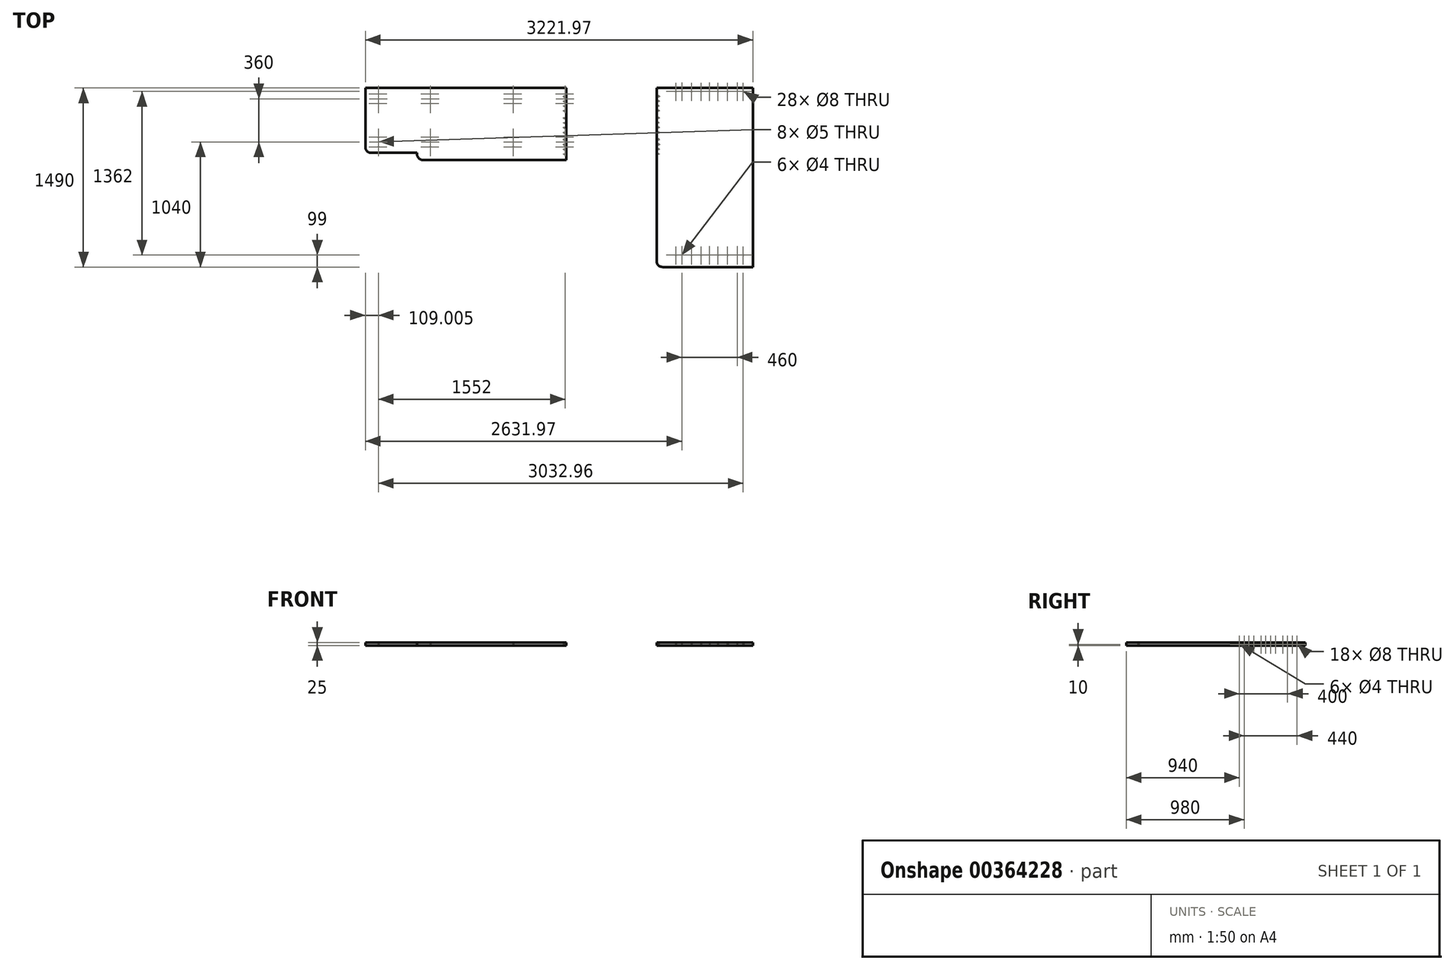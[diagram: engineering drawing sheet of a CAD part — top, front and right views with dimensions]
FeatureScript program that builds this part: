
annotation { "Feature Type Name" : "Feature", "Feature Type Description" : "" }
export const myFeature = defineFeature(function(context is Context, id is Id, definition is map)
    precondition{}
    {
        {
            var Q0;
            Q0=qCreatedBy(makeId("Top.planeOp"),FACE);
            var sketch = newSketch(context, id + "F0", { "sketchPlane" : qUnion([Q0])});
            skLineSegment(sketch, "E0.bottom", {"start": v(-2341.59, 0) * mm, "end": v(-671.59, 0) * mm});
            skLineSegment(sketch, "E0.left", {"start": v(-2341.59, 0) * mm, "end": v(-2341.59, -490) * mm});
            skLineSegment(sketch, "E0.right", {"start": v(-671.59, 0) * mm, "end": v(-671.59, -600) * mm});
            skLineSegment(sketch, "E1", {"start": v(-671.59, -600) * mm, "end": v(-1861.59, -600) * mm});
            skLineSegment(sketch, "E2", {"start": v(-2291.59, -540) * mm, "end": v(-1911.59, -540) * mm});
            skLineSegment(sketch, "E3", {"start": v(-1911.59, -540) * mm, "end": v(-1911.59, -550) * mm});
            skPoint(sketch, "E4.visualSharp", {"position": v(-2341.59, -540) * mm});
            skArc(sketch, "E4.filletArc", {"start": v(-2341.59, -490) * mm, "mid": v(-2326.94, -525.36) * mm, "end": v(-2291.59, -540) * mm});
            skPoint(sketch, "E5.visualSharp", {"position": v(-1911.59, -600) * mm});
            skArc(sketch, "E5.filletArc", {"start": v(-1911.59, -550) * mm, "mid": v(-1896.94, -585.36) * mm, "end": v(-1861.59, -600) * mm});
            skLineSegment(sketch, "E6", {"start": v(0, 0) * mm, "end": v(-671.59, 0) * mm, "construction": true});
            skSolve(sketch);
        }
        {
            var Q0;
            Q0=qCreatedBy(makeId("Top.planeOp"),FACE);
            var sketch = newSketch(context, id + "F1", { "sketchPlane" : qUnion([Q0])});
            skLineSegment(sketch, "E7.bottom", {"start": v(80.38, 0) * mm, "end": v(880.38, 0) * mm});
            skLineSegment(sketch, "E7.top", {"start": v(130.38, -1490) * mm, "end": v(880.38, -1490) * mm});
            skLineSegment(sketch, "E7.left", {"start": v(80.38, 0) * mm, "end": v(80.38, -1440) * mm});
            skLineSegment(sketch, "E7.right", {"start": v(880.38, 0) * mm, "end": v(880.38, -1490) * mm});
            skPoint(sketch, "E8.visualSharp", {"position": v(80.38, -1490) * mm});
            skArc(sketch, "E8.filletArc", {"start": v(80.38, -1440) * mm, "mid": v(95.02, -1475.36) * mm, "end": v(130.38, -1490) * mm});
            skLineSegment(sketch, "E9", {"start": v(0, 0) * mm, "end": v(80.38, 0) * mm, "construction": true});
            skSolve(sketch);
        }
        {
            var Q0;
            Q0=makeQuery(id+"F0.imprint","IMPRINT",FACE,{"disambiguationData":[TD([[makeQuery(id+"F0.imprint","IMPRINT",EDGE,{"derivedFrom":sQuery(id+"F0.wireOp",EDGE,"E0.bottom")}),-1.0]])]});
            extrude(context, id + "F2", {"entities" : qUnion([Q0]), "depth" : 25 * mm});
        }
        {
            var Q0;
            Q0 = qSketchRegion(id + "F1", true);
            extrude(context, id + "F3", {"entities" : qUnion([Q0]), "depth" : 25 * mm});
        }
        {
            var Q0;
            Q0=makeQuery(id+"F2.opExtrude","CAP_FACE",FACE,{"disambiguationData":[OSD([sQuery(id+"F0.wireOp",EDGE,"E0.bottom"),sQuery(id+"F0.wireOp",EDGE,"E0.left"),sQuery(id+"F0.wireOp",EDGE,"E0.right"),sQuery(id+"F0.wireOp",EDGE,"E1"),sQuery(id+"F0.wireOp",EDGE,"E2"),sQuery(id+"F0.wireOp",EDGE,"E3"),sQuery(id+"F0.wireOp",EDGE,"E4.filletArc"),sQuery(id+"F0.wireOp",EDGE,"E5.filletArc")])],"isStart":true});
            var sketch = newSketch(context, id + "F4", { "sketchPlane" : qUnion([Q0])});
            skLineSegment(sketch, "E10", {"start": v(-680.59, 600) * mm, "end": v(-680.59, 0) * mm, "construction": true});
            skPoint(sketch, "E11", {"position": v(-680.59, 50) * mm});
            skPoint(sketch, "E12.0.1.0", {"position": v(-680.59, 90) * mm});
            skPoint(sketch, "E12.0.2.0", {"position": v(-680.59, 130) * mm});
            skPoint(sketch, "E12.1.0.0", {"position": v(-1112.59, 50) * mm});
            skPoint(sketch, "E12.1.1.0", {"position": v(-1112.59, 90) * mm});
            skPoint(sketch, "E12.1.2.0", {"position": v(-1112.59, 130) * mm});
            skLineSegment(sketch, "E12.direction1", {"start": v(-680.59, 50) * mm, "end": v(-1112.59, 50) * mm, "construction": true});
            skLineSegment(sketch, "E12.direction2", {"start": v(-680.59, 50) * mm, "end": v(-680.59, 90) * mm, "construction": true});
            skLineSegment(sketch, "E13.0.1.0", {"start": v(-680.59, 410) * mm, "end": v(-1112.59, 410) * mm, "construction": true});
            skLineSegment(sketch, "E13.0.1.1", {"start": v(-680.59, 410) * mm, "end": v(-680.59, 450) * mm, "construction": true});
            skPoint(sketch, "E13.0.1.2", {"position": v(-680.59, 410) * mm});
            skPoint(sketch, "E13.0.1.3", {"position": v(-680.59, 450) * mm});
            skPoint(sketch, "E13.0.1.4", {"position": v(-680.59, 490) * mm});
            skPoint(sketch, "E13.0.1.5", {"position": v(-1112.59, 410) * mm});
            skPoint(sketch, "E13.0.1.6", {"position": v(-1112.59, 450) * mm});
            skPoint(sketch, "E13.0.1.7", {"position": v(-1112.59, 490) * mm});
            skLineSegment(sketch, "E13.1.0.0", {"start": v(-1800.59, 50) * mm, "end": v(-2232.59, 50) * mm, "construction": true});
            skLineSegment(sketch, "E13.1.0.1", {"start": v(-1800.59, 50) * mm, "end": v(-1800.59, 90) * mm, "construction": true});
            skPoint(sketch, "E13.1.0.2", {"position": v(-1800.59, 50) * mm});
            skPoint(sketch, "E13.1.0.3", {"position": v(-1800.59, 90) * mm});
            skPoint(sketch, "E13.1.0.4", {"position": v(-1800.59, 130) * mm});
            skPoint(sketch, "E13.1.0.5", {"position": v(-2232.59, 50) * mm});
            skPoint(sketch, "E13.1.0.6", {"position": v(-2232.59, 90) * mm});
            skPoint(sketch, "E13.1.0.7", {"position": v(-2232.59, 130) * mm});
            skLineSegment(sketch, "E13.1.1.0", {"start": v(-1800.59, 410) * mm, "end": v(-2232.59, 410) * mm, "construction": true});
            skLineSegment(sketch, "E13.1.1.1", {"start": v(-1800.59, 410) * mm, "end": v(-1800.59, 450) * mm, "construction": true});
            skPoint(sketch, "E13.1.1.2", {"position": v(-1800.59, 410) * mm});
            skPoint(sketch, "E13.1.1.3", {"position": v(-1800.59, 450) * mm});
            skPoint(sketch, "E13.1.1.4", {"position": v(-1800.59, 490) * mm});
            skPoint(sketch, "E13.1.1.5", {"position": v(-2232.59, 410) * mm});
            skPoint(sketch, "E13.1.1.6", {"position": v(-2232.59, 450) * mm});
            skPoint(sketch, "E13.1.1.7", {"position": v(-2232.59, 490) * mm});
            skLineSegment(sketch, "E13.direction1", {"start": v(-1112.59, 50) * mm, "end": v(-2232.59, 50) * mm, "construction": true});
            skLineSegment(sketch, "E13.direction2", {"start": v(-1112.59, 50) * mm, "end": v(-1112.59, 410) * mm, "construction": true});
            skSolve(sketch);
        }
        {
            var Q0;
            Q0=sQuery(id+"F4.wireOp",VERTEX,"E13.1.1.7");
            var Q1;
            Q1=sQuery(id+"F4.wireOp",VERTEX,"E13.1.1.5");
            var Q2;
            Q2=sQuery(id+"F4.wireOp",VERTEX,"E13.1.1.4");
            var Q3;
            Q3=sQuery(id+"F4.wireOp",VERTEX,"E13.1.1.2");
            var Q4;
            Q4=sQuery(id+"F4.wireOp",VERTEX,"E13.1.0.4");
            var Q5;
            Q5=sQuery(id+"F4.wireOp",VERTEX,"E13.1.0.2");
            var Q6;
            Q6=sQuery(id+"F4.wireOp",VERTEX,"E13.1.0.5");
            var Q7;
            Q7=sQuery(id+"F4.wireOp",VERTEX,"E13.1.0.7");
            var Q8;
            Q8=sQuery(id+"F4.wireOp",VERTEX,"E13.0.1.7");
            var Q9;
            Q9=sQuery(id+"F4.wireOp",VERTEX,"E13.0.1.5");
            var Q10;
            Q10=sQuery(id+"F4.wireOp",VERTEX,"E12.1.2.0");
            var Q11;
            Q11=sQuery(id+"F4.wireOp",VERTEX,"E12.1.0.0");
            var Q12;
            Q12=sQuery(id+"F4.wireOp",VERTEX,"E11");
            var Q13;
            Q13=sQuery(id+"F4.wireOp",VERTEX,"E12.0.2.0");
            var Q14;
            Q14=sQuery(id+"F4.wireOp",VERTEX,"E13.0.1.2");
            var Q15;
            Q15=sQuery(id+"F4.wireOp",VERTEX,"E13.0.1.4");
            var Q16;
            Q16=makeQuery(id+"F2.opExtrude","SWEPT_BODY",BODY,{"disambiguationData":[OSD([sQuery(id+"F0.wireOp",EDGE,"E0.bottom"),sQuery(id+"F0.wireOp",EDGE,"E0.left"),sQuery(id+"F0.wireOp",EDGE,"E0.right"),sQuery(id+"F0.wireOp",EDGE,"E1"),sQuery(id+"F0.wireOp",EDGE,"E2"),sQuery(id+"F0.wireOp",EDGE,"E3"),sQuery(id+"F0.wireOp",EDGE,"E4.filletArc"),sQuery(id+"F0.wireOp",EDGE,"E5.filletArc")])]});
            hole(context, id + "F5", {"style" : HoleStyle.SIMPLE, "endStyle" : HoleEndStyle.BLIND, "holeDiameter" : 8 * mm, "holeDepth" : 15 * mm, "isTappedThrough" : true, "tappedDepth" : 12 * mm, "tapClearance" : 3, "startFromSketch" : true, "locations" : qUnion([Q0, Q1, Q2, Q3, Q4, Q5, Q6, Q7, Q8, Q9, Q10, Q11, Q12, Q13, Q14, Q15]), "scope" : qUnion([Q16])});
        }
        {
            var Q0;
            Q0=sQuery(id+"F4.wireOp",VERTEX,"E13.1.1.6");
            var Q1;
            Q1=sQuery(id+"F4.wireOp",VERTEX,"E13.1.1.3");
            var Q2;
            Q2=sQuery(id+"F4.wireOp",VERTEX,"E13.1.0.3");
            var Q3;
            Q3=sQuery(id+"F4.wireOp",VERTEX,"E13.1.0.6");
            var Q4;
            Q4=sQuery(id+"F4.wireOp",VERTEX,"E13.0.1.6");
            var Q5;
            Q5=sQuery(id+"F4.wireOp",VERTEX,"E13.0.1.3");
            var Q6;
            Q6=sQuery(id+"F4.wireOp",VERTEX,"E12.0.1.0");
            var Q7;
            Q7=sQuery(id+"F4.wireOp",VERTEX,"E12.1.1.0");
            var Q8;
            Q8=makeQuery(id+"F2.opExtrude","SWEPT_BODY",BODY,{"disambiguationData":[OSD([sQuery(id+"F0.wireOp",EDGE,"E0.bottom"),sQuery(id+"F0.wireOp",EDGE,"E0.left"),sQuery(id+"F0.wireOp",EDGE,"E0.right"),sQuery(id+"F0.wireOp",EDGE,"E1"),sQuery(id+"F0.wireOp",EDGE,"E2"),sQuery(id+"F0.wireOp",EDGE,"E3"),sQuery(id+"F0.wireOp",EDGE,"E4.filletArc"),sQuery(id+"F0.wireOp",EDGE,"E5.filletArc")])]});
            hole(context, id + "F6", {"style" : HoleStyle.SIMPLE, "endStyle" : HoleEndStyle.BLIND, "holeDiameter" : 5 * mm, "holeDepth" : 10 * mm, "isTappedThrough" : true, "tappedDepth" : 12 * mm, "tapClearance" : 3, "startFromSketch" : true, "locations" : qUnion([Q0, Q1, Q2, Q3, Q4, Q5, Q6, Q7]), "scope" : qUnion([Q8])});
        }
        {
            var Q0;
            Q0=makeQuery(id+"F2.opExtrude","SWEPT_FACE",FACE,{"disambiguationData":[OSD([sQuery(id+"F0.wireOp",EDGE,"E0.right")])]});
            var sketch = newSketch(context, id + "F7", { "sketchPlane" : qUnion([Q0])});
            skLineSegment(sketch, "E14.bottom", {"start": v(-600, 25) * mm, "end": v(0, 25) * mm});
            skLineSegment(sketch, "E14.top", {"start": v(-600, 0) * mm, "end": v(0, 0) * mm});
            skLineSegment(sketch, "E14.left", {"start": v(-600, 25) * mm, "end": v(-600, 0) * mm});
            skLineSegment(sketch, "E14.right", {"start": v(0, 25) * mm, "end": v(0, 0) * mm});
            skLineSegment(sketch, "E15", {"start": v(-600, 10) * mm, "end": v(0, 10) * mm, "construction": true});
            skPoint(sketch, "E16", {"position": v(-70, 10) * mm});
            skPoint(sketch, "E17.1.0.0", {"position": v(-110, 10) * mm});
            skPoint(sketch, "E17.2.0.0", {"position": v(-150, 10) * mm});
            skPoint(sketch, "E17.3.0.0", {"position": v(-190, 10) * mm});
            skLineSegment(sketch, "E17.direction1", {"start": v(-70, 10) * mm, "end": v(-110, 10) * mm, "construction": true});
            skLineSegment(sketch, "E18.1.0.0", {"start": v(-250, 10) * mm, "end": v(-290, 10) * mm, "construction": true});
            skPoint(sketch, "E18.1.0.1", {"position": v(-330, 10) * mm});
            skPoint(sketch, "E18.1.0.2", {"position": v(-250, 10) * mm});
            skPoint(sketch, "E18.1.0.3", {"position": v(-290, 10) * mm});
            skPoint(sketch, "E18.1.0.4", {"position": v(-370, 10) * mm});
            skLineSegment(sketch, "E18.direction1", {"start": v(-190, 10) * mm, "end": v(-370, 10) * mm, "construction": true});
            skLineSegment(sketch, "E19.0.2.0", {"start": v(-430, 10) * mm, "end": v(-470, 10) * mm, "construction": true});
            skPoint(sketch, "E19.3.2.0", {"position": v(-510, 10) * mm});
            skPoint(sketch, "E19.4.2.0", {"position": v(-430, 10) * mm});
            skPoint(sketch, "E19.5.2.0", {"position": v(-470, 10) * mm});
            skPoint(sketch, "E19.6.2.0", {"position": v(-550, 10) * mm});
            skSolve(sketch);
        }
        {
            var Q0;
            Q0=sQuery(id+"F7.wireOp",VERTEX,"E19.3.2.0");
            var Q1;
            Q1=sQuery(id+"F7.wireOp",VERTEX,"E19.5.2.0");
            var Q2;
            Q2=sQuery(id+"F7.wireOp",VERTEX,"E19.4.2.0");
            var Q3;
            Q3=sQuery(id+"F7.wireOp",VERTEX,"E18.1.0.4");
            var Q4;
            Q4=sQuery(id+"F7.wireOp",VERTEX,"E18.1.0.1");
            var Q5;
            Q5=sQuery(id+"F7.wireOp",VERTEX,"E18.1.0.2");
            var Q6;
            Q6=sQuery(id+"F7.wireOp",VERTEX,"E17.3.0.0");
            var Q7;
            Q7=sQuery(id+"F7.wireOp",VERTEX,"E17.1.0.0");
            var Q8;
            Q8=sQuery(id+"F7.wireOp",VERTEX,"E16");
            var Q9;
            Q9=makeQuery(id+"F2.opExtrude","SWEPT_BODY",BODY,{"disambiguationData":[OSD([sQuery(id+"F0.wireOp",EDGE,"E0.bottom"),sQuery(id+"F0.wireOp",EDGE,"E0.left"),sQuery(id+"F0.wireOp",EDGE,"E0.right"),sQuery(id+"F0.wireOp",EDGE,"E1"),sQuery(id+"F0.wireOp",EDGE,"E2"),sQuery(id+"F0.wireOp",EDGE,"E3"),sQuery(id+"F0.wireOp",EDGE,"E4.filletArc"),sQuery(id+"F0.wireOp",EDGE,"E5.filletArc")])]});
            hole(context, id + "F8", {"style" : HoleStyle.SIMPLE, "endStyle" : HoleEndStyle.BLIND, "holeDiameter" : 8 * mm, "holeDepth" : 20 * mm, "isTappedThrough" : true, "tappedDepth" : 12 * mm, "tapClearance" : 3, "startFromSketch" : true, "locations" : qUnion([Q0, Q1, Q2, Q3, Q4, Q5, Q6, Q7, Q8]), "scope" : qUnion([Q9])});
        }
        {
            var Q0;
            Q0=sQuery(id+"F7.wireOp",VERTEX,"E17.2.0.0");
            var Q1;
            Q1=sQuery(id+"F7.wireOp",VERTEX,"E18.1.0.3");
            var Q2;
            Q2=sQuery(id+"F7.wireOp",VERTEX,"E19.6.2.0");
            var Q3;
            Q3=makeQuery(id+"F2.opExtrude","SWEPT_BODY",BODY,{"disambiguationData":[OSD([sQuery(id+"F0.wireOp",EDGE,"E0.bottom"),sQuery(id+"F0.wireOp",EDGE,"E0.left"),sQuery(id+"F0.wireOp",EDGE,"E0.right"),sQuery(id+"F0.wireOp",EDGE,"E1"),sQuery(id+"F0.wireOp",EDGE,"E2"),sQuery(id+"F0.wireOp",EDGE,"E3"),sQuery(id+"F0.wireOp",EDGE,"E4.filletArc"),sQuery(id+"F0.wireOp",EDGE,"E5.filletArc")])]});
            hole(context, id + "F9", {"style" : HoleStyle.SIMPLE, "endStyle" : HoleEndStyle.BLIND, "holeDiameter" : 4 * mm, "holeDepth" : 20 * mm, "isTappedThrough" : true, "tappedDepth" : 12 * mm, "tapClearance" : 3, "startFromSketch" : true, "locations" : qUnion([Q0, Q1, Q2]), "scope" : qUnion([Q3])});
        }
        {
            var Q0;
            Q0=sQuery(id+"F7.wireOp",VERTEX,"E19.3.2.0");
            var Q1;
            Q1=sQuery(id+"F7.wireOp",VERTEX,"E19.5.2.0");
            var Q2;
            Q2=sQuery(id+"F7.wireOp",VERTEX,"E19.4.2.0");
            var Q3;
            Q3=sQuery(id+"F7.wireOp",VERTEX,"E18.1.0.4");
            var Q4;
            Q4=sQuery(id+"F7.wireOp",VERTEX,"E18.1.0.1");
            var Q5;
            Q5=sQuery(id+"F7.wireOp",VERTEX,"E18.1.0.0.start");
            var Q6;
            Q6=sQuery(id+"F7.wireOp",VERTEX,"E17.3.0.0");
            var Q7;
            Q7=sQuery(id+"F7.wireOp",VERTEX,"E17.1.0.0");
            var Q8;
            Q8=sQuery(id+"F7.wireOp",VERTEX,"E16");
            var Q9;
            Q9=makeQuery(id+"F3.opExtrude","SWEPT_BODY",BODY,{"disambiguationData":[OSD([sQuery(id+"F1.wireOp",EDGE,"E7.bottom"),sQuery(id+"F1.wireOp",EDGE,"E7.top"),sQuery(id+"F1.wireOp",EDGE,"E7.left"),sQuery(id+"F1.wireOp",EDGE,"E7.right"),sQuery(id+"F1.wireOp",EDGE,"E8.filletArc")])]});
            hole(context, id + "F10", {"style" : HoleStyle.SIMPLE, "endStyle" : HoleEndStyle.BLIND, "oppositeDirection" : true, "holeDiameter" : 8 * mm, "holeDepth" : 20 * mm, "isTappedThrough" : true, "tappedDepth" : 12 * mm, "tapClearance" : 3, "locations" : qUnion([Q0, Q1, Q2, Q3, Q4, Q5, Q6, Q7, Q8]), "scope" : qUnion([Q9])});
        }
        {
            var Q0;
            Q0=sQuery(id+"F7.wireOp",VERTEX,"E18.1.0.3");
            var Q1;
            Q1=sQuery(id+"F7.wireOp",VERTEX,"E17.2.0.0");
            var Q2;
            Q2=sQuery(id+"F7.wireOp",VERTEX,"E19.6.2.0");
            var Q3;
            Q3=makeQuery(id+"F3.opExtrude","SWEPT_BODY",BODY,{"disambiguationData":[OSD([sQuery(id+"F1.wireOp",EDGE,"E7.bottom"),sQuery(id+"F1.wireOp",EDGE,"E7.top"),sQuery(id+"F1.wireOp",EDGE,"E7.left"),sQuery(id+"F1.wireOp",EDGE,"E7.right"),sQuery(id+"F1.wireOp",EDGE,"E8.filletArc")])]});
            hole(context, id + "F11", {"style" : HoleStyle.SIMPLE, "endStyle" : HoleEndStyle.BLIND, "oppositeDirection" : true, "holeDiameter" : 4 * mm, "holeDepth" : 20 * mm, "isTappedThrough" : true, "tappedDepth" : 12 * mm, "tapClearance" : 3, "locations" : qUnion([Q0, Q1, Q2]), "scope" : qUnion([Q3])});
        }
        {
            var Q0;
            Q0=makeQuery(id+"F1.imprint","IMPRINT",FACE,{"disambiguationData":[TD([[makeQuery(id+"F1.imprint","IMPRINT",EDGE,{"derivedFrom":sQuery(id+"F1.wireOp",EDGE,"E7.bottom")}),-1.0]])]});
            var sketch = newSketch(context, id + "F12", { "sketchPlane" : qUnion([Q0])});
            skLineSegment(sketch, "E20", {"start": v(80.38, -1391) * mm, "end": v(880.38, -1391) * mm, "construction": true});
            skPoint(sketch, "E21", {"position": v(800.38, -1391) * mm});
            skPoint(sketch, "E22", {"position": v(750.38, -1391) * mm});
            skPoint(sketch, "E23", {"position": v(670.38, -1391) * mm});
            skPoint(sketch, "E24", {"position": v(520.38, -1391) * mm});
            skPoint(sketch, "E25", {"position": v(590.38, -1391) * mm});
            skLineSegment(sketch, "E26", {"start": v(520.38, -1469.86) * mm, "end": v(520.38, -1312.14) * mm, "construction": true});
            skPoint(sketch, "E27.MirrorP", {"position": v(450.38, -1391) * mm});
            skPoint(sketch, "E28.MirrorP", {"position": v(370.38, -1391) * mm});
            skPoint(sketch, "E29.MirrorP", {"position": v(290.38, -1391) * mm});
            skPoint(sketch, "E30.MirrorP", {"position": v(240.38, -1391) * mm});
            skLineSegment(sketch, "E31", {"start": v(-56.04, -710) * mm, "end": v(972.9, -710) * mm, "construction": true});
            skLineSegment(sketch, "E32", {"start": v(-112.91, -29) * mm, "end": v(989.87, -29) * mm, "construction": true});
            skPoint(sketch, "E33.MirrorP", {"position": v(240.38, -29) * mm});
            skPoint(sketch, "E34.MirrorP", {"position": v(290.38, -29) * mm});
            skPoint(sketch, "E35.MirrorP", {"position": v(370.38, -29) * mm});
            skPoint(sketch, "E36.MirrorP", {"position": v(450.38, -29) * mm});
            skPoint(sketch, "E37.MirrorP", {"position": v(520.38, -29) * mm});
            skPoint(sketch, "E38.MirrorP", {"position": v(590.38, -29) * mm});
            skPoint(sketch, "E39.MirrorP", {"position": v(670.38, -29) * mm});
            skPoint(sketch, "E40.MirrorP", {"position": v(800.38, -29) * mm});
            skPoint(sketch, "E41.MirrorP", {"position": v(750.38, -29) * mm});
            skSolve(sketch);
        }
        {
            var Q0;
            Q0=sQuery(id+"F12.wireOp",VERTEX,"E22");
            var Q1;
            Q1=sQuery(id+"F12.wireOp",VERTEX,"E24");
            var Q2;
            Q2=sQuery(id+"F12.wireOp",VERTEX,"E29.MirrorP");
            var Q3;
            Q3=sQuery(id+"F12.wireOp",VERTEX,"E34.MirrorP");
            var Q4;
            Q4=sQuery(id+"F12.wireOp",VERTEX,"E37.MirrorP");
            var Q5;
            Q5=sQuery(id+"F12.wireOp",VERTEX,"E41.MirrorP");
            var Q6;
            Q6=makeQuery(id+"F3.opExtrude","SWEPT_BODY",BODY,{"disambiguationData":[OSD([sQuery(id+"F1.wireOp",EDGE,"E7.bottom"),sQuery(id+"F1.wireOp",EDGE,"E7.top"),sQuery(id+"F1.wireOp",EDGE,"E7.left"),sQuery(id+"F1.wireOp",EDGE,"E7.right"),sQuery(id+"F1.wireOp",EDGE,"E8.filletArc")])]});
            hole(context, id + "F13", {"style" : HoleStyle.SIMPLE, "endStyle" : HoleEndStyle.BLIND, "oppositeDirection" : true, "holeDiameter" : 4 * mm, "holeDepth" : 20 * mm, "isTappedThrough" : true, "tappedDepth" : 12 * mm, "tapClearance" : 3, "locations" : qUnion([Q0, Q1, Q2, Q3, Q4, Q5]), "scope" : qUnion([Q6])});
        }
        {
            var Q0;
            Q0=sQuery(id+"F12.wireOp",VERTEX,"E21");
            var Q1;
            Q1=sQuery(id+"F12.wireOp",VERTEX,"E23");
            var Q2;
            Q2=sQuery(id+"F12.wireOp",VERTEX,"E25");
            var Q3;
            Q3=sQuery(id+"F12.wireOp",VERTEX,"E27.MirrorP");
            var Q4;
            Q4=sQuery(id+"F12.wireOp",VERTEX,"E28.MirrorP");
            var Q5;
            Q5=sQuery(id+"F12.wireOp",VERTEX,"E30.MirrorP");
            var Q6;
            Q6=sQuery(id+"F12.wireOp",VERTEX,"E33.MirrorP");
            var Q7;
            Q7=sQuery(id+"F12.wireOp",VERTEX,"E35.MirrorP");
            var Q8;
            Q8=sQuery(id+"F12.wireOp",VERTEX,"E36.MirrorP");
            var Q9;
            Q9=sQuery(id+"F12.wireOp",VERTEX,"E38.MirrorP");
            var Q10;
            Q10=sQuery(id+"F12.wireOp",VERTEX,"E39.MirrorP");
            var Q11;
            Q11=sQuery(id+"F12.wireOp",VERTEX,"E40.MirrorP");
            var Q12;
            Q12=makeQuery(id+"F3.opExtrude","SWEPT_BODY",BODY,{"disambiguationData":[OSD([sQuery(id+"F1.wireOp",EDGE,"E7.bottom"),sQuery(id+"F1.wireOp",EDGE,"E7.top"),sQuery(id+"F1.wireOp",EDGE,"E7.left"),sQuery(id+"F1.wireOp",EDGE,"E7.right"),sQuery(id+"F1.wireOp",EDGE,"E8.filletArc")])]});
            hole(context, id + "F14", {"style" : HoleStyle.SIMPLE, "endStyle" : HoleEndStyle.BLIND, "oppositeDirection" : true, "holeDiameter" : 8 * mm, "holeDepth" : 20 * mm, "isTappedThrough" : true, "tappedDepth" : 12 * mm, "tapClearance" : 3, "locations" : qUnion([Q0, Q1, Q2, Q3, Q4, Q5, Q6, Q7, Q8, Q9, Q10, Q11]), "scope" : qUnion([Q12])});
        }
    });
